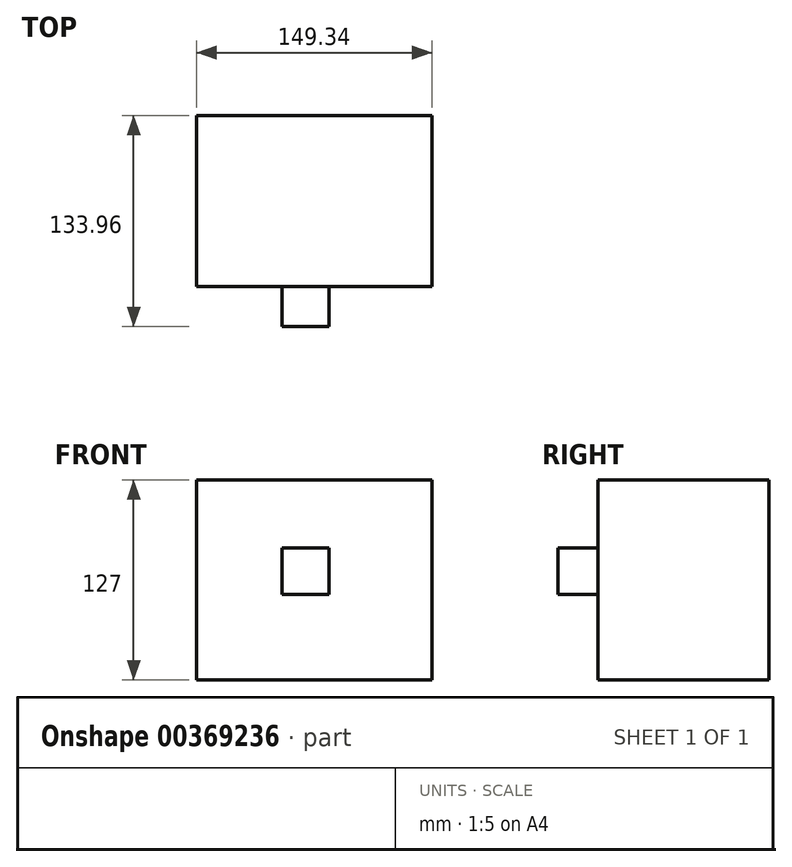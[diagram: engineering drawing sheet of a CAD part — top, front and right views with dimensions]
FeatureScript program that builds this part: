
annotation { "Feature Type Name" : "Feature", "Feature Type Description" : "" }
export const myFeature = defineFeature(function(context is Context, id is Id, definition is map)
    precondition{}
    {
        {
            var Q0;
            Q0=qCreatedBy(makeId("Top.planeOp"),FACE);
            var sketch = newSketch(context, id + "F0", { "sketchPlane" : qUnion([Q0])});
            skLineSegment(sketch, "E0.bottom", {"start": v(-54.28, 31.64) * mm, "end": v(95.06, 31.64) * mm});
            skLineSegment(sketch, "E0.top", {"start": v(-54.28, -76.92) * mm, "end": v(95.06, -76.92) * mm});
            skLineSegment(sketch, "E0.left", {"start": v(-54.28, 31.64) * mm, "end": v(-54.28, -76.92) * mm});
            skLineSegment(sketch, "E0.right", {"start": v(95.06, 31.64) * mm, "end": v(95.06, -76.92) * mm});
            skSolve(sketch);
        }
        {
            var Q0;
            Q0=makeQuery(id+"F0.imprint","IMPRINT",FACE,{"disambiguationData":[TD([[makeQuery(id+"F0.imprint","IMPRINT",EDGE,{"derivedFrom":sQuery(id+"F0.wireOp",EDGE,"E0.bottom")}),-1.0]])]});
            extrude(context, id + "F1", {"entities" : qUnion([Q0]), "depth" : 127 * mm});
        }
        {
            var Q0;
            Q0=makeQuery(id+"F1.opExtrude","SWEPT_FACE",FACE,{"disambiguationData":[OSD([sQuery(id+"F0.wireOp",EDGE,"E0.top")])]});
            var sketch = newSketch(context, id + "F2", { "sketchPlane" : qUnion([Q0])});
            skCircle(sketch, "E1", {"center": v(15.64, 68) * mm, "radius": 43.75 * mm});
            skSolve(sketch);
        }
        {
            var Q0;
            Q0=makeQuery(id+"F2.imprint","IMPRINT",FACE,{"disambiguationData":[TD([[makeQuery(id+"F2.imprint","IMPRINT",EDGE,{"derivedFrom":sQuery(id+"F2.wireOp",EDGE,"E1")}),1.0]])]});
            var sketch = newSketch(context, id + "F3", { "sketchPlane" : qUnion([Q0])});
            skLineSegment(sketch, "E2.bottom", {"start": v(0, 83.94) * mm, "end": v(29.75, 83.94) * mm});
            skLineSegment(sketch, "E2.top", {"start": v(0, 54.32) * mm, "end": v(29.75, 54.32) * mm});
            skLineSegment(sketch, "E2.left", {"start": v(0, 83.94) * mm, "end": v(0, 54.32) * mm});
            skLineSegment(sketch, "E2.right", {"start": v(29.75, 83.94) * mm, "end": v(29.75, 54.32) * mm});
            skSolve(sketch);
        }
        {
            var Q0;
            Q0 = qSketchRegion(id + "F3", true);
            extrude(context, id + "F4", {"entities" : qUnion([Q0]), "operationType" : NewBodyOperationType.ADD, "depth" : 25.4 * mm});
        }
    });
